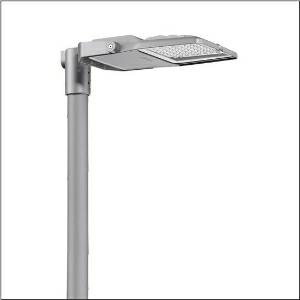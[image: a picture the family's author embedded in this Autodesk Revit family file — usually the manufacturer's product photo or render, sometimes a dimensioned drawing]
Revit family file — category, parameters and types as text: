
# Revit family: floodlight_fl_21_iq_mini___pl61_5xa7772b2c3a_0206
name_source: partatom
category: Lighting Fixtures
units: mm (PartAtom-declared; Revit-internal decimal feet)

## family parameters
Cut with Voids When Loaded = No
Host = Face
Light Source = No
Part Type = Normal
Room Calculation Point = No
Round Connector Dimension = Use Diameter
Shared = No

## types (1)
- --- (1 x LED, 6120 lm, 45.5 W, 3000K)
    Apparent Load = 46 VA
    CIE Flux Codes = 33 65 98 100 100
    Color Rendering = 70
    Color Temperature = 3000K
    Default Elevation = 1800 mm
    Description = Floodlight FL 21 iQ mini, floodlight, primary light control with lens, of PMMA, primary optical cover: protective disc, of toughened safety glass, transparent, light distribution: PL61, light emission: direct distribution, installation type: surface-mounted, lamps: LED, High Power LED, rated values: 6.120lm | 45,5W | 134,5lm/W (begin service life); end service life: 6.120lm | 48W; at 50% lumin. flux: 3.060lm | 21,5W | 142,3lm/W, colour temperature: 3000K, colour rendering: CRI > 70, light colour: 730, light setting 1 begin service life: 100% | 6.120lm | 45,5W | 134,5lm/W | 3.000K, light setting 1 end service life: 48W, further light settings possible, control: pre-setting: linear dimming characteristic, Auto-Match, Temp-Guard, Night-Set, Smart-Wire, Desk-Remote (wireless, voltage-free reading and setting of iQ features in the workshop via application-optimized NFC function/RFID function), optimised constant luminous flux control (CLO 2.0), Light-Fading, Lumen-Switch, with terminal, 6-pole, mains connection: 220..240V, AC, 50/60Hz, luminaire housing, of diecast aluminium, powder-coated, SITECO metallic grey (DB 702S), corrosivity category C5 mid according to DIN EN ISO 12944suitable for swimming poolschlorine-resistant, sealing non-destructively replaceable, please order mast flange separately, mast bracket, of steel, galvanised, powder-coated, protection rating (complete): IP66, insulation class (complete): insulation class II (safety insulation), certification: CE, ENEC, VDE, protection symbol: D, impact resistance: IK08, permissible operating ambient temperature: -40..+40°C, permissible operating ambient temperature for outdoor applications: -40..+50°C, standard: DIN EN 12944, LABS conformity tested according to VDMA 24364:2018-05, packaging unit: 1 piece

Light Distribution: PL61
    Height = 70 mm
    Lamp = 1 x LED
    Lamp Light Flux = 6120 lm
    Lamp Power = 45.5 W
    Lamp count = 1
    Length = 485 mm
    Luminous efficacy = 135 lm/W
    Manufacturer = Siteco
    ModVariant = No
    Model = 5XA7772B2C3A
    Number of Poles = 1
    OnlyDefault = Yes
    Power Factor = 1
    Product Name = Floodlight FL 21 iQ mini | PL61
    Product group = floodlight | pylon annexe
    ProductGroupID = 6201
    Protection Class = Protection class II
    Protection Degree = IP 66
    RLX_Detail_Level = 1
    RLX_Emergency_Light_Flux = 0 lm
    RLX_Emergency_Type = 0
    RLX_Emergency_Type_DB = No
    RlxData = <blob elided: 101457 chars, md5=8f1fd45c>
    Socket = socket
    Standby Power = 0 W
    System Light Flux = 6120 lm
    System Power = 46 W
    Type Comments = factory setting: luminous flux: 100 % | dim-lin: 254 | 463 mA
    Type Image = l_1007125.jpg
    URL = http://relux.com
    VarID = @adj_173069
    Voltage = 0 V
    Weight = 0.00 kg
    Width = 337 mm

## geometry (parser evidence)
native form markers: Blend x4, Sweep x13
no freeform markers — native parametric forms only
